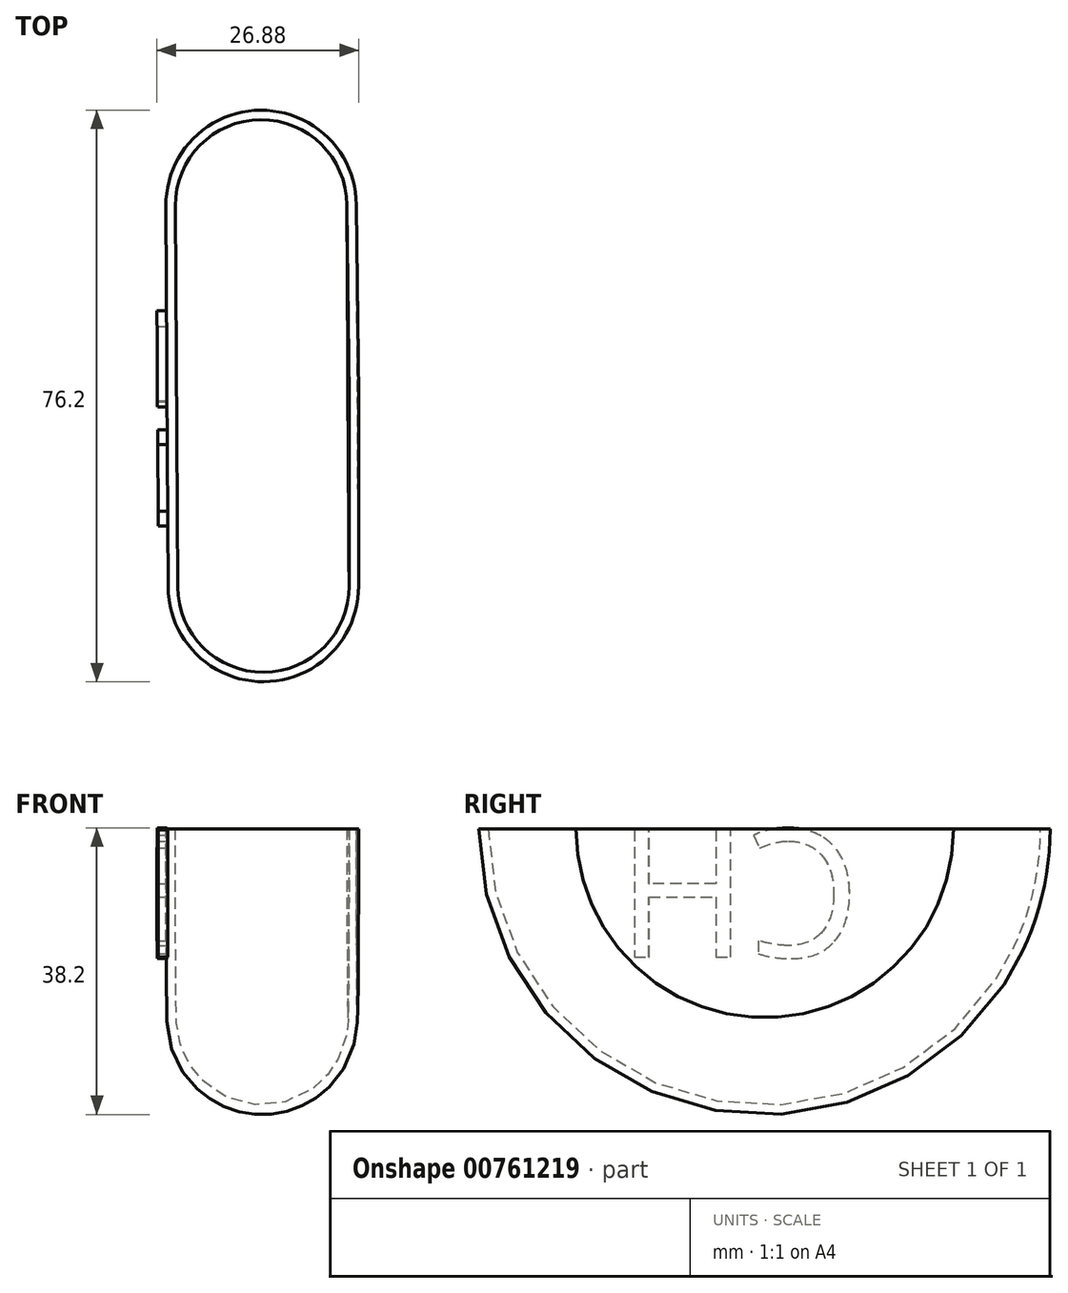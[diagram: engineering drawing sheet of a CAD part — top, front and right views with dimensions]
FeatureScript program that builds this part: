
annotation { "Feature Type Name" : "Feature", "Feature Type Description" : "" }
export const myFeature = defineFeature(function(context is Context, id is Id, definition is map)
    precondition{}
    {
        {
            var Q0;
            Q0=qCreatedBy(makeId("Top.planeOp"),FACE);
            var sketch = newSketch(context, id + "F0", { "sketchPlane" : qUnion([Q0])});
            skArc(sketch, "E0", {"start": v(-53.47, -55.8) * mm, "mid": v(-40.58, -68.43) * mm, "end": v(-28.07, -55.43) * mm});
            skLineSegment(sketch, "E1", {"start": v(-53.47, -55.8) * mm, "end": v(-53.62, -30.4) * mm});
            skLineSegment(sketch, "E2", {"start": v(-28.07, -55.43) * mm, "end": v(-28.07, -30.26) * mm});
            skArc(sketch, "E3", {"start": v(-28.07, -4.7) * mm, "mid": v(-28.07, -4.67) * mm, "end": v(-28.07, -4.63) * mm});
            skPoint(sketch, "E3.third.point", {"position": v(-38.33, -17.25) * mm});
            skLineSegment(sketch, "E4", {"start": v(-53.62, -30.4) * mm, "end": v(-28.07, -30.26) * mm});
            skPoint(sketch, "E5.orphan", {"position": v(-53.77, -5) * mm});
            skLineSegment(sketch, "E6.trimOffspring", {"start": v(-28.07, -4.7) * mm, "end": v(-28.07, -4.63) * mm});
            skSolve(sketch);
        }
        {
            var Q0;
            Q0=makeQuery(id+"F0.imprint","IMPRINT",FACE,{"disambiguationData":[TD([[makeQuery(id+"F0.imprint","IMPRINT",EDGE,{"derivedFrom":sQuery(id+"F0.wireOp",EDGE,"E0")}),1.0]])]});
            var Q1;
            Q1=sQuery(id+"F0.wireOp",EDGE,"E4");
            revolve(context, id + "F1", {"surfaceOperationType" : NewSurfaceOperationType.NEW, "entities" : qUnion([Q0]), "axis" : qUnion([Q1]), "revolveType" : RevolveType.ONE_DIRECTION, "angle" : 180 * degree});
        }
        {
            var Q0;
            Q0=makeQuery(id+"F1.opRevolve","CAP_FACE",FACE,{"disambiguationData":[OSD([sQuery(id+"F0.wireOp",EDGE,"E0"),sQuery(id+"F0.wireOp",EDGE,"E1"),sQuery(id+"F0.wireOp",EDGE,"E2"),sQuery(id+"F0.wireOp",EDGE,"E4")])],"isStart":true});
            shell(context, id + "F2", {"entities" : qUnion([Q0]), "thickness" : 1.27 * mm});
        }
        {
            var Q0;
            Q0=makeQuery(id+"F1.opRevolve","SWEPT_FACE",FACE,{"disambiguationData":[OSD([sQuery(id+"F0.wireOp",EDGE,"E1")])]});
            var sketch = newSketch(context, id + "F3", { "sketchPlane" : qUnion([Q0])});
            skText(sketch, "E7", { "text": "CH", "fontName": "OpenSans-Regular.ttf"});
            const initialGuessF3  = {"E7": [0.0172, -0.01708, 1, 0, 0.01708]};
            skSetInitialGuess(sketch, initialGuessF3);
            skSolve(sketch);
        }
        {
            var Q0;
            Q0 = qSketchRegion(id + "F3", true);
            extrude(context, id + "F4", {"entities" : qUnion([Q0]), "operationType" : NewBodyOperationType.ADD, "depth" : 1.27 * mm, "offsetDistance" : 25.4 * mm});
        }
    });
